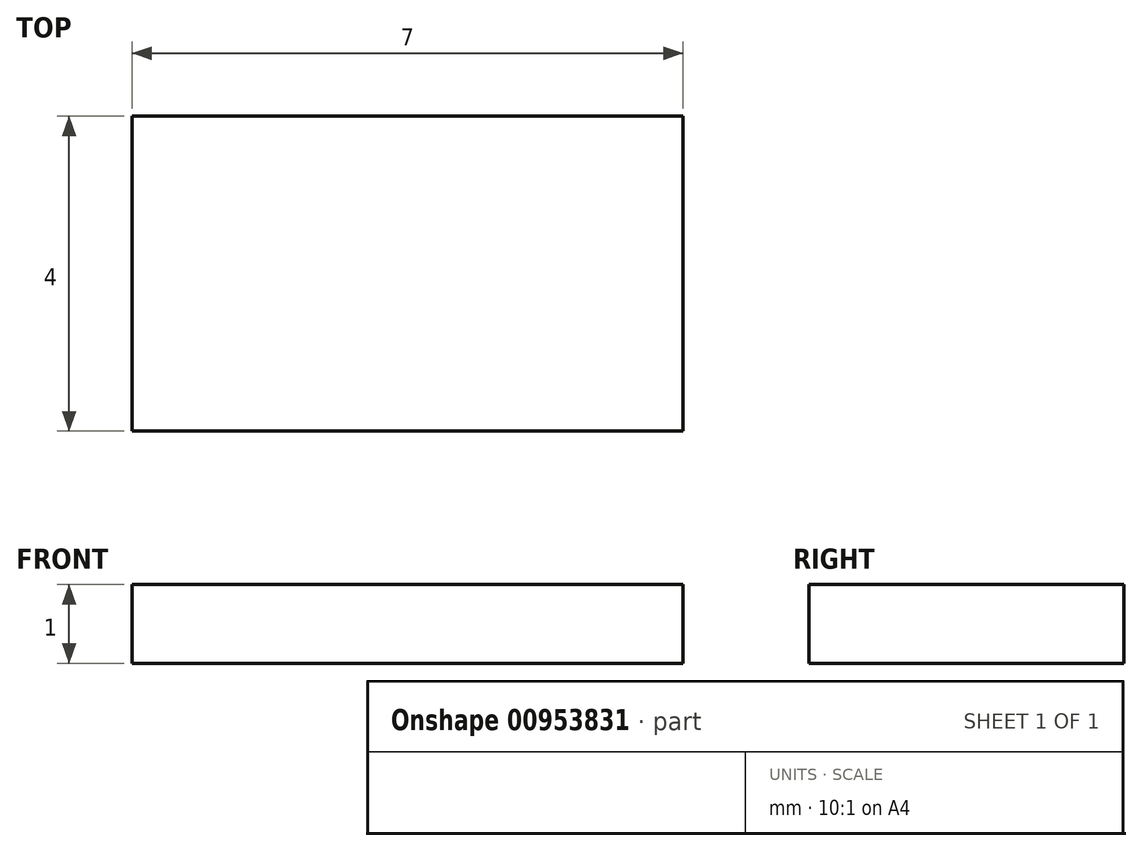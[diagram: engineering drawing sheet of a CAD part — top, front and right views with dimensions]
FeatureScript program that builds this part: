
annotation { "Feature Type Name" : "Feature", "Feature Type Description" : "" }
export const myFeature = defineFeature(function(context is Context, id is Id, definition is map)
    precondition{}
    {
        {
            var Q0;
            Q0=qCreatedBy(makeId("Top.planeOp"),FACE);
            var sketch = newSketch(context, id + "F0", { "sketchPlane" : qUnion([Q0])});
            skLineSegment(sketch, "E0.bottom", {"start": v(0, 0) * mm, "end": v(7, 0) * mm});
            skLineSegment(sketch, "E0.top", {"start": v(0, 4) * mm, "end": v(7, 4) * mm});
            skLineSegment(sketch, "E0.left", {"start": v(0, 0) * mm, "end": v(0, 4) * mm});
            skLineSegment(sketch, "E0.right", {"start": v(7, 0) * mm, "end": v(7, 4) * mm});
            skSolve(sketch);
        }
        {
            var Q0;
            Q0=makeQuery(id+"F0.imprint","IMPRINT",FACE,{"disambiguationData":[TD([[makeQuery(id+"F0.imprint","IMPRINT",EDGE,{"derivedFrom":sQuery(id+"F0.wireOp",EDGE,"E0.bottom")}),1.0]])]});
            extrude(context, id + "F1", {"entities" : qUnion([Q0]), "depth" : 1 * mm, "offsetDistance" : 25 * mm});
        }
    });
